# Revit family: M_層板燈 - 線性方形
name_source: partatom
category: Lighting Fixtures
revit_build: Autodesk Revit 2017 (Build: 20160109_1515(x64)
units: mm (PartAtom-declared; Revit-internal decimal feet)

## family parameters
Cut with Voids When Loaded = No
Host = Face
Light Source = Yes
OmniClass Number = 23.80.70.11.11
OmniClass Title = General Luminaries, Non Directional
Part Type = Normal
Room Calculation Point = No
Round Connector Dimension = Use Diameter
Shared = No

## types (8) — shared parameters
Assembly Code = D5020210
Color Filter = 16777215
Default Elevation = 1200 mm  [stored 3.93701 ft]
Dimming Lamp Color Temperature Shift = <None>
Emit Shape Visible in Rendering = No
Lamp = T-12
Tilt Angle = -90.00°
分佈口材料 = 玻璃，白色，高亮度
燈箱材料 = 鋼，油漆塗層，象牙白，亮面
穩壓器極數 = 1
負載分類 = 照明 - 住宅單元

## per-type parameters (varying)
| type | Apparent Load | Emit from Rectangle Length | Emit from Rectangle Width | Photometric Web File | 寬度 1 | 方塊寬度 | 穩壓器電壓 | 箱長度 | 長度1 |
| 0300x1200mm (1 燈) - 120V | 40 VA | 1174 mm  [stored 3.85171 ft] | 274 mm  [stored 0.89895 ft] | 1x41T12.ies | 150 mm  [stored 0.492126 ft] | 300 mm  [stored 0.984252 ft] | 120 V | 1200 mm  [stored 3.93701 ft] | 600 mm  [stored 1.9685 ft] |
| 0300x1200mm (1 燈) - 277V | 40 VA | 1174 mm  [stored 3.85171 ft] | 274 mm  [stored 0.89895 ft] | 1x41T12.ies | 150 mm  [stored 0.492126 ft] | 300 mm  [stored 0.984252 ft] | 277 V | 1200 mm  [stored 3.93701 ft] | 600 mm  [stored 1.9685 ft] |
| 0300x1200mm (2 燈) - 120V | 80 VA | 1174 mm  [stored 3.85171 ft] | 274 mm  [stored 0.89895 ft] | 1x42A12.ies | 150 mm  [stored 0.492126 ft] | 300 mm  [stored 0.984252 ft] | 120 V | 1200 mm  [stored 3.93701 ft] | 600 mm  [stored 1.9685 ft] |
| 0300x1200mm (2 燈) - 277V | 80 VA | 1174 mm  [stored 3.85171 ft] | 274 mm  [stored 0.89895 ft] | 1x42A12.ies | 150 mm  [stored 0.492126 ft] | 300 mm  [stored 0.984252 ft] | 277 V | 1200 mm  [stored 3.93701 ft] | 600 mm  [stored 1.9685 ft] |
| 0600x0600mm (2 燈) - 120V | 40 VA | 574 mm | 574 mm | 2x22T12.ies | 300 mm  [stored 0.984252 ft] | 600 mm  [stored 1.9685 ft] | 120 V | 600 mm  [stored 1.9685 ft] | 300 mm  [stored 0.984252 ft] |
| 0600x0600mm (2 燈) - 277V | 40 VA | 574 mm | 574 mm | 2x22T12.ies | 300 mm  [stored 0.984252 ft] | 600 mm  [stored 1.9685 ft] | 277 V | 600 mm  [stored 1.9685 ft] | 300 mm  [stored 0.984252 ft] |
| 0600x1200mm (2 燈) - 120V | 80 VA | 1174 mm  [stored 3.85171 ft] | 574 mm | 2x42T12.ies | 300 mm  [stored 0.984252 ft] | 600 mm  [stored 1.9685 ft] | 120 V | 1200 mm  [stored 3.93701 ft] | 600 mm  [stored 1.9685 ft] |
| 0600x1200mm (2 燈) - 277V | 80 VA | 1174 mm  [stored 3.85171 ft] | 574 mm | 2x42T12.ies | 300 mm  [stored 0.984252 ft] | 600 mm  [stored 1.9685 ft] | 277 V | 1200 mm  [stored 3.93701 ft] | 600 mm  [stored 1.9685 ft] |

note: [stored X ft] marks values corroborated as IEEE doubles in the binary element streams (Revit-internal decimal feet)
